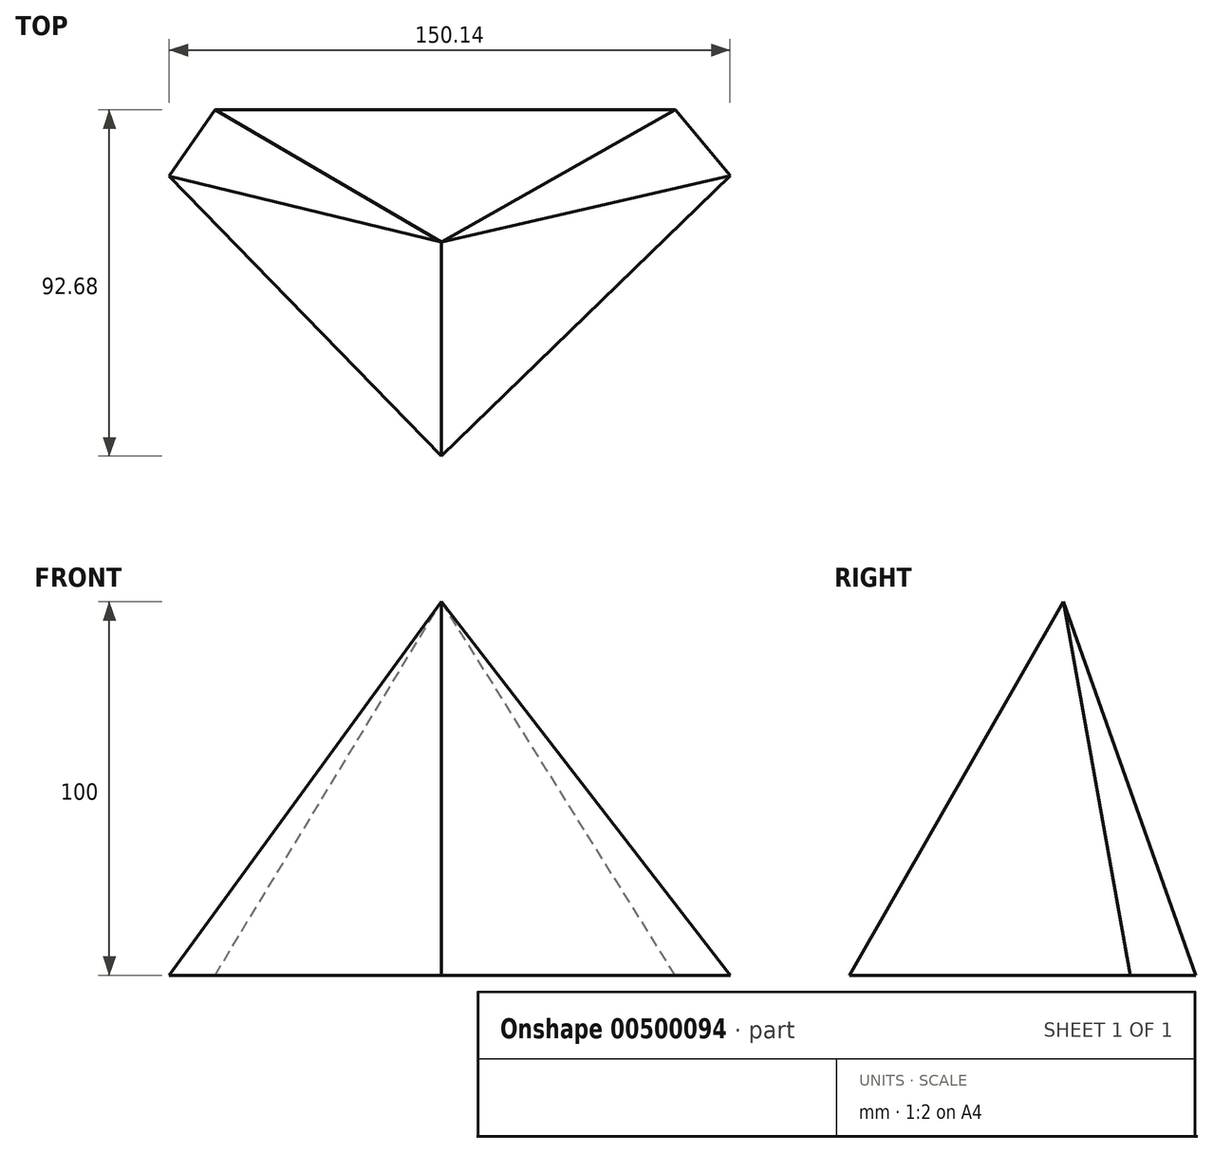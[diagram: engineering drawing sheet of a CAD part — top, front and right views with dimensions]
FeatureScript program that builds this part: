
annotation { "Feature Type Name" : "Feature", "Feature Type Description" : "" }
export const myFeature = defineFeature(function(context is Context, id is Id, definition is map)
    precondition{}
    {
        {
            var Q0;
            Q0=qCreatedBy(makeId("Top.planeOp"),FACE);
            var sketch = newSketch(context, id + "F0", { "sketchPlane" : qUnion([Q0])});
            skLineSegment(sketch, "E0", {"start": v(-60.63, 35.41) * mm, "end": v(62.57, 35.41) * mm});
            skLineSegment(sketch, "E1", {"start": v(62.57, 35.41) * mm, "end": v(77.25, 17.86) * mm});
            skLineSegment(sketch, "E2", {"start": v(77.25, 17.86) * mm, "end": v(0, -57.27) * mm});
            skLineSegment(sketch, "E3", {"start": v(0, -57.27) * mm, "end": v(-72.9, 17.68) * mm});
            skLineSegment(sketch, "E4", {"start": v(-72.9, 17.68) * mm, "end": v(-60.63, 35.41) * mm});
            skSolve(sketch);
        }
        {
            var Q0;
            Q0=qCreatedBy(makeId("Top.planeOp"),FACE);
            cPlane(context, id + "F1", {"entities" : qUnion([Q0]), "cplaneType" : CPlaneType.OFFSET, "offset" : 100 * mm, "width" : 152.4 * mm, "height" : 152.4 * mm});
        }
        {
            var Q0;
            Q0=qCreatedBy(id+"F1.planeOp",FACE);
            var sketch = newSketch(context, id + "F2", { "sketchPlane" : qUnion([Q0])});
            skPoint(sketch, "E5", {"position": v(0, 0) * mm});
            skSolve(sketch);
        }
        {
            var Q0;
            Q0=makeQuery(id+"F0.imprint","IMPRINT",FACE,{"disambiguationData":[TD([[makeQuery(id+"F0.imprint","IMPRINT",EDGE,{"derivedFrom":sQuery(id+"F0.wireOp",EDGE,"E0")}),-1.0]])]});
            var Q1;
            Q1=sQuery(id+"F2.wireOp",VERTEX,"E5");
            loft(context, id + "F3", {"sheetProfilesArray" : [{ "sheetProfileEntities" : qUnion([Q0]) }, { "sheetProfileEntities" : qUnion([Q1]) }]});
        }
    });
